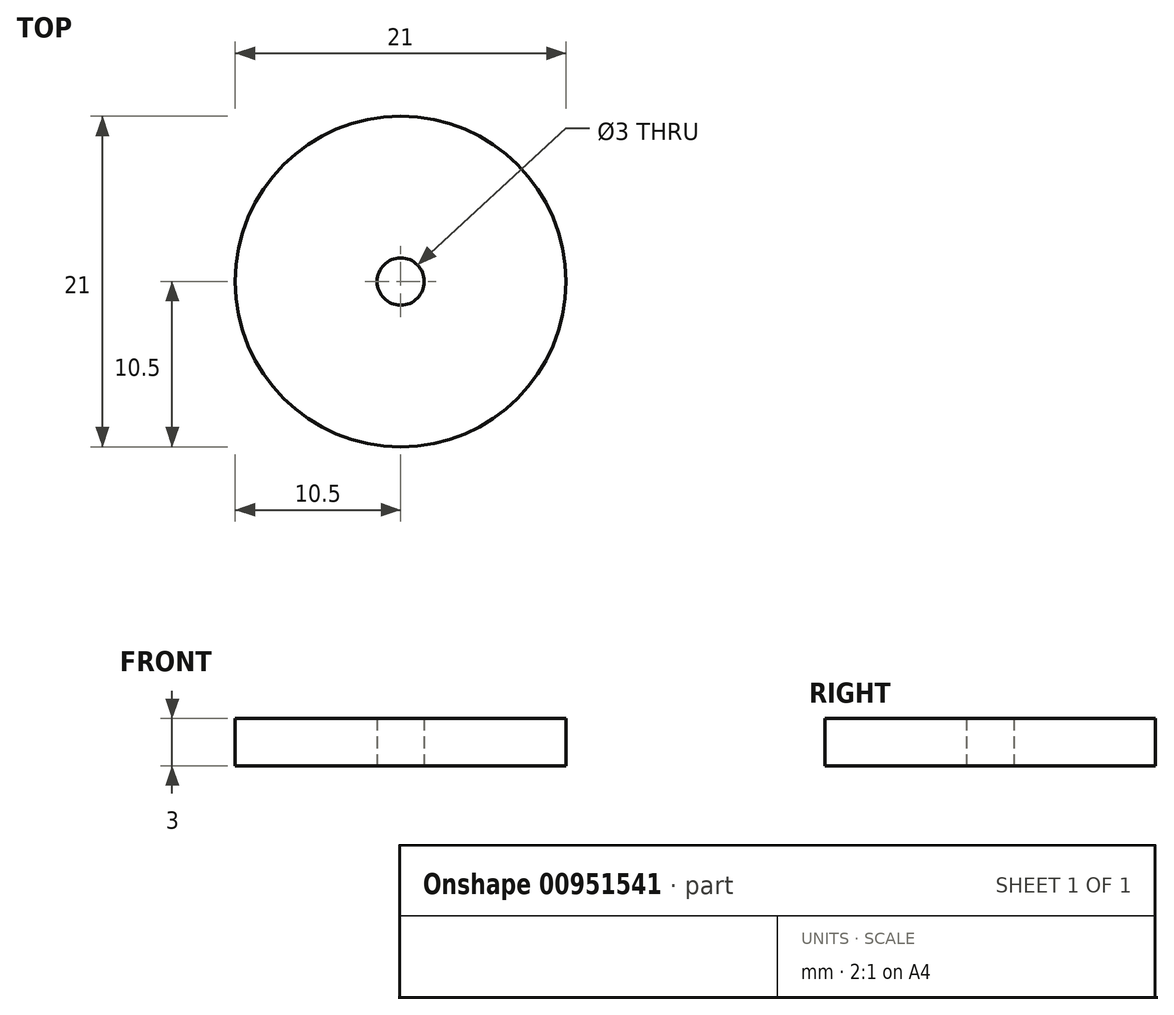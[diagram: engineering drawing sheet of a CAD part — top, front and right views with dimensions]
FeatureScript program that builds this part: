
annotation { "Feature Type Name" : "Feature", "Feature Type Description" : "" }
export const myFeature = defineFeature(function(context is Context, id is Id, definition is map)
    precondition{}
    {
        {
            var Q0;
            Q0=qCreatedBy(makeId("Top.planeOp"),FACE);
            var sketch = newSketch(context, id + "F0", { "sketchPlane" : qUnion([Q0])});
            skCircle(sketch, "E0", {"center": v(0, 0) * mm, "radius": 10.5 * mm});
            skCircle(sketch, "E1", {"center": v(0, 0) * mm, "radius": 1.5 * mm});
            skSolve(sketch);
        }
        {
            var Q0;
            Q0 = qSketchRegion(id + "F0", true);
            extrude(context, id + "F1", {"entities" : qUnion([Q0]), "depth" : 3 * mm, "offsetDistance" : 25 * mm});
        }
    });
